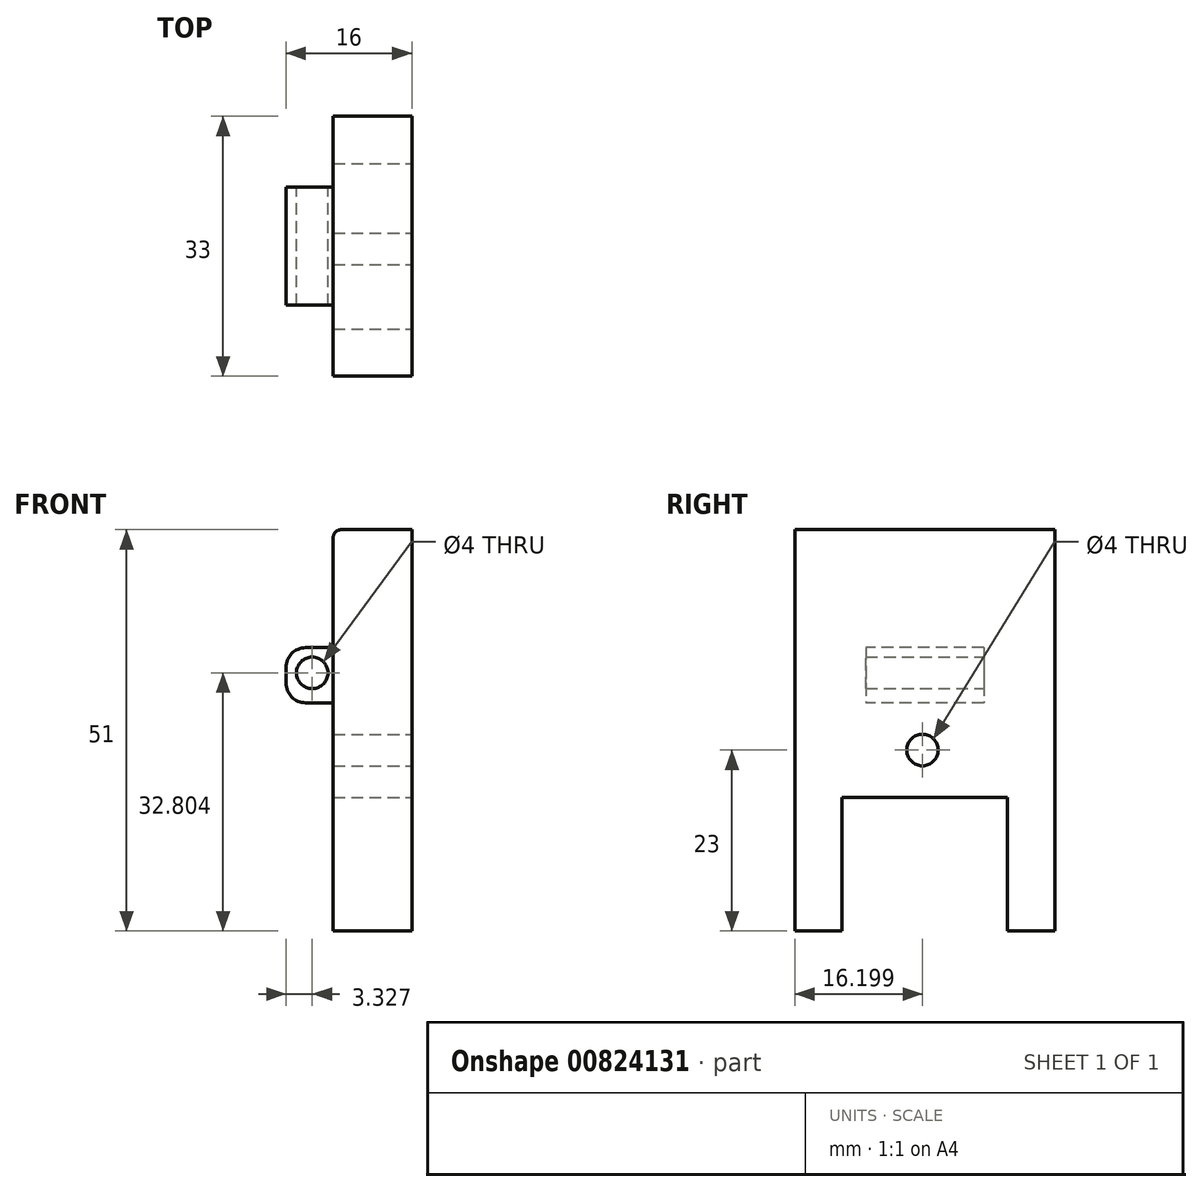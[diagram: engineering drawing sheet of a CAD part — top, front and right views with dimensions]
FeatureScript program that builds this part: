
annotation { "Feature Type Name" : "Feature", "Feature Type Description" : "" }
export const myFeature = defineFeature(function(context is Context, id is Id, definition is map)
    precondition{}
    {
        {
            var Q0;
            Q0=qCreatedBy(makeId("Right.planeOp"),FACE);
            var sketch = newSketch(context, id + "F0", { "sketchPlane" : qUnion([Q0])});
            skLineSegment(sketch, "E0.bottom", {"start": v(0, 0) * mm, "end": v(6, 0) * mm});
            skLineSegment(sketch, "E0.top", {"start": v(0, 51) * mm, "end": v(33, 51) * mm});
            skLineSegment(sketch, "E0.left", {"start": v(0, 0) * mm, "end": v(0, 51) * mm});
            skLineSegment(sketch, "E0.right", {"start": v(33, 0) * mm, "end": v(33, 51) * mm});
            skLineSegment(sketch, "E1.bottom", {"start": v(6, 17) * mm, "end": v(27, 17) * mm});
            skLineSegment(sketch, "E1.left", {"start": v(6, 17) * mm, "end": v(6, 0) * mm});
            skLineSegment(sketch, "E1.right", {"start": v(27, 17) * mm, "end": v(27, 0) * mm});
            skLineSegment(sketch, "E2.trimOffspring", {"start": v(27, 0) * mm, "end": v(33, 0) * mm});
            skCircle(sketch, "E3", {"center": v(16.2, 23) * mm, "radius": 2 * mm});
            skSolve(sketch);
        }
        {
            var Q0;
            Q0 = qSketchRegion(id + "F0", true);
            extrude(context, id + "F1", {"entities" : qUnion([Q0]), "oppositeDirection" : true, "depth" : 10 * mm, "offsetDistance" : 25.4 * mm});
        }
        {
            var Q0;
            Q0=makeQuery(id+"F1.opExtrude","CAP_EDGE",EDGE,{"disambiguationData":[OSD([sQuery(id+"F0.wireOp",EDGE,"E0.top")])],"isStart":false});
            fillet(context, id + "F2", {"entities" : qUnion([Q0]), "radius" : 1 * mm, "tangentPropagation" : true, "allowEdgeOverflow" : false});
        }
        {
            var Q0;
            Q0=makeQuery(id+"F1.opExtrude","CAP_FACE",FACE,{"disambiguationData":[OSD([sQuery(id+"F0.wireOp",EDGE,"E0.bottom"),sQuery(id+"F0.wireOp",EDGE,"E0.top"),sQuery(id+"F0.wireOp",EDGE,"E0.left"),sQuery(id+"F0.wireOp",EDGE,"E0.right"),sQuery(id+"F0.wireOp",EDGE,"E1.bottom"),sQuery(id+"F0.wireOp",EDGE,"E1.left"),sQuery(id+"F0.wireOp",EDGE,"E1.right"),sQuery(id+"F0.wireOp",EDGE,"E2.trimOffspring"),sQuery(id+"F0.wireOp",EDGE,"E3")])],"isStart":false});
            var sketch = newSketch(context, id + "F3", { "sketchPlane" : qUnion([Q0])});
            skLineSegment(sketch, "E4.bottom", {"start": v(-24, 36) * mm, "end": v(-9, 36) * mm});
            skLineSegment(sketch, "E4.top", {"start": v(-24, 29) * mm, "end": v(-9, 29) * mm});
            skLineSegment(sketch, "E4.left", {"start": v(-24, 36) * mm, "end": v(-24, 29) * mm});
            skLineSegment(sketch, "E4.right", {"start": v(-9, 36) * mm, "end": v(-9, 29) * mm});
            skSolve(sketch);
        }
        {
            var Q0;
            Q0 = qSketchRegion(id + "F3", true);
            extrude(context, id + "F4", {"entities" : qUnion([Q0]), "operationType" : NewBodyOperationType.ADD, "depth" : 6 * mm, "offsetDistance" : 25.4 * mm});
        }
        {
            var Q0;
            Q0=makeQuery(id+"F4.opExtrude","CAP_EDGE",EDGE,{"disambiguationData":[OSD([sQuery(id+"F3.wireOp",EDGE,"E4.bottom")])],"isStart":false});
            var Q1;
            Q1=makeQuery(id+"F4.opExtrude","CAP_EDGE",EDGE,{"disambiguationData":[OSD([sQuery(id+"F3.wireOp",EDGE,"E4.top")])],"isStart":false});
            fillet(context, id + "F5", {"entities" : qUnion([Q0, Q1]), "radius" : 2.5 * mm, "tangentPropagation" : true, "allowEdgeOverflow" : false});
        }
        {
            var Q0;
            Q0=makeQuery(id+"F4.opExtrude","SWEPT_FACE",FACE,{"disambiguationData":[OSD([sQuery(id+"F3.wireOp",EDGE,"E4.left")])]});
            var sketch = newSketch(context, id + "F6", { "sketchPlane" : qUnion([Q0])});
            skCircle(sketch, "E5", {"center": v(12.67, 32.8) * mm, "radius": 2 * mm});
            skSolve(sketch);
        }
        {
            var Q0;
            Q0 = qSketchRegion(id + "F6", true);
            extrude(context, id + "F7", {"entities" : qUnion([Q0]), "operationType" : NewBodyOperationType.REMOVE, "oppositeDirection" : true, "depth" : 25.4 * mm, "offsetDistance" : 25.4 * mm});
        }
    });
